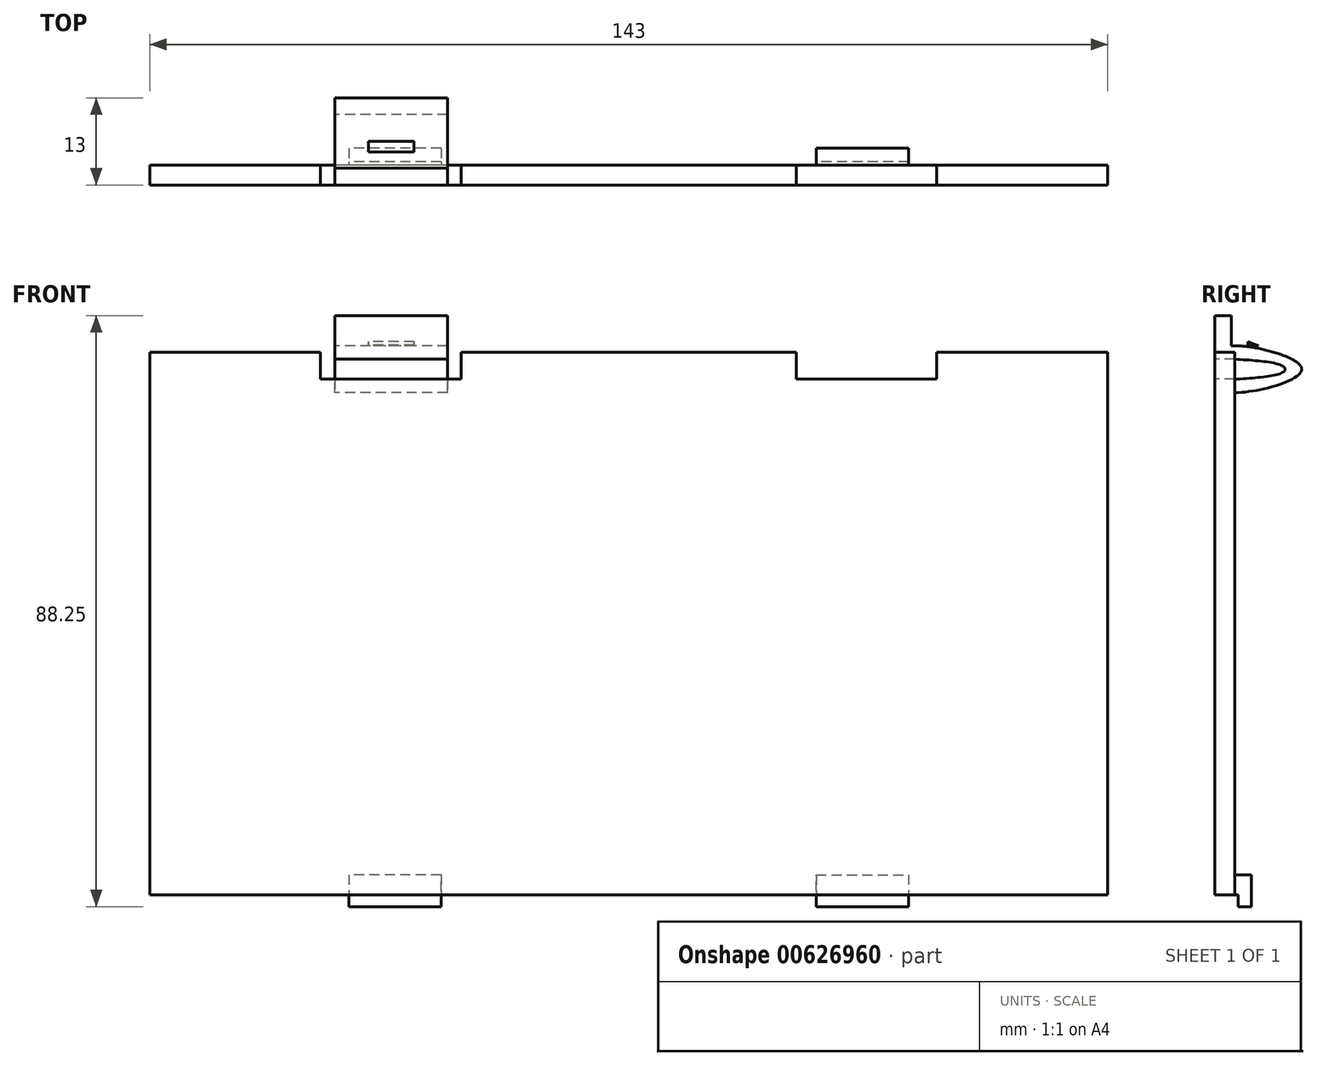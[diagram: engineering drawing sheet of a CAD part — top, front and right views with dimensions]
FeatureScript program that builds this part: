
annotation { "Feature Type Name" : "Feature", "Feature Type Description" : "" }
export const myFeature = defineFeature(function(context is Context, id is Id, definition is map)
    precondition{}
    {
        {
            var Q0;
            Q0=qCreatedBy(makeId("Front.planeOp"),FACE);
            var sketch = newSketch(context, id + "F0", { "sketchPlane" : qUnion([Q0])});
            skLineSegment(sketch, "E0.bottom", {"start": v(71.5, 40.5) * mm, "end": v(-71.5, 40.5) * mm});
            skLineSegment(sketch, "E0.top", {"start": v(71.5, -40.5) * mm, "end": v(-71.5, -40.5) * mm});
            skLineSegment(sketch, "E0.left", {"start": v(71.5, 40.5) * mm, "end": v(71.5, -40.5) * mm});
            skLineSegment(sketch, "E0.right", {"start": v(-71.5, 40.5) * mm, "end": v(-71.5, -40.5) * mm});
            skPoint(sketch, "E0.middle", {"position": v(0, 0) * mm});
            skSolve(sketch);
        }
        {
            var Q0;
            Q0=makeQuery(id+"F0.imprint","IMPRINT",FACE,{"disambiguationData":[TD([[makeQuery(id+"F0.imprint","IMPRINT",EDGE,{"derivedFrom":sQuery(id+"F0.wireOp",EDGE,"E0.bottom")}),1.0]])]});
            extrude(context, id + "F1", {"entities" : qUnion([Q0]), "depth" : 3 * mm});
        }
        {
            var Q0;
            Q0=makeQuery(id+"F1.opExtrude","CAP_FACE",FACE,{"disambiguationData":[OSD([sQuery(id+"F0.wireOp",EDGE,"E0.bottom"),sQuery(id+"F0.wireOp",EDGE,"E0.top"),sQuery(id+"F0.wireOp",EDGE,"E0.left"),sQuery(id+"F0.wireOp",EDGE,"E0.right")])],"isStart":true});
            var sketch = newSketch(context, id + "F2", { "sketchPlane" : qUnion([Q0])});
            skLineSegment(sketch, "E1", {"start": v(-28, -40.5) * mm, "end": v(-28, 40.5) * mm, "construction": true});
            skLineSegment(sketch, "E2", {"start": v(-28, 0) * mm, "end": v(0, 0) * mm, "construction": true});
            skLineSegment(sketch, "E3", {"start": v(0, 0) * mm, "end": v(28, 0) * mm, "construction": true});
            skLineSegment(sketch, "E4", {"start": v(28, 40.5) * mm, "end": v(28, -40.5) * mm, "construction": true});
            skLineSegment(sketch, "E5", {"start": v(-28, -37.5) * mm, "end": v(-41.8, -37.5) * mm});
            skLineSegment(sketch, "E6", {"start": v(-41.8, -37.5) * mm, "end": v(-41.8, -40.5) * mm});
            skLineSegment(sketch, "E7", {"start": v(-41.8, -40.5) * mm, "end": v(-28, -40.5) * mm});
            skLineSegment(sketch, "E8", {"start": v(-28, -37.5) * mm, "end": v(-28, -40.5) * mm});
            skLineSegment(sketch, "E9.MirrorCS", {"start": v(41.8, -40.5) * mm, "end": v(28, -40.5) * mm});
            skLineSegment(sketch, "E10.MirrorCS", {"start": v(41.8, -37.5) * mm, "end": v(41.8, -40.5) * mm});
            skLineSegment(sketch, "E11.MirrorCS", {"start": v(28, -37.5) * mm, "end": v(41.8, -37.5) * mm});
            skLineSegment(sketch, "E12", {"start": v(28, -37.5) * mm, "end": v(28, -40.5) * mm});
            skSolve(sketch);
        }
        {
            var Q0;
            Q0=makeQuery(id+"F2.imprint","IMPRINT",FACE,{"disambiguationData":[TD([[makeQuery(id+"F2.imprint","IMPRINT",EDGE,{"derivedFrom":sQuery(id+"F2.wireOp",EDGE,"E5")}),1.0]])]});
            var Q1;
            Q1=makeQuery(id+"F2.imprint","IMPRINT",FACE,{"disambiguationData":[TD([[makeQuery(id+"F2.imprint","IMPRINT",EDGE,{"derivedFrom":sQuery(id+"F2.wireOp",EDGE,"E9.MirrorCS")}),1.0]])]});
            extrude(context, id + "F3", {"entities" : qUnion([Q0, Q1]), "operationType" : NewBodyOperationType.ADD, "depth" : 0.5 * mm});
        }
        {
            var Q0;
            Q0=makeQuery(id+"F3.opExtrude","CAP_FACE",FACE,{"disambiguationData":[OSD([sQuery(id+"F2.wireOp",EDGE,"E5"),sQuery(id+"F2.wireOp",EDGE,"E6"),sQuery(id+"F2.wireOp",EDGE,"E7"),sQuery(id+"F2.wireOp",EDGE,"E8")])],"isStart":false});
            var sketch = newSketch(context, id + "F4", { "sketchPlane" : qUnion([Q0])});
            skLineSegment(sketch, "E13.0", {"start": v(-28, -37.5) * mm, "end": v(-41.8, -37.5) * mm});
            skLineSegment(sketch, "E14", {"start": v(-41.8, -37.5) * mm, "end": v(-41.8, -42.25) * mm});
            skLineSegment(sketch, "E15", {"start": v(-41.8, -42.25) * mm, "end": v(-28, -42.25) * mm});
            skLineSegment(sketch, "E16", {"start": v(-28, -42.25) * mm, "end": v(-28, -37.5) * mm});
            skLineSegment(sketch, "E17.MirrorCS", {"start": v(28, -42.25) * mm, "end": v(28, -37.5) * mm});
            skLineSegment(sketch, "E18.MirrorCS", {"start": v(28, -37.5) * mm, "end": v(41.8, -37.5) * mm});
            skLineSegment(sketch, "E19.MirrorCS", {"start": v(41.8, -42.25) * mm, "end": v(28, -42.25) * mm});
            skLineSegment(sketch, "E20.MirrorCS", {"start": v(41.8, -37.5) * mm, "end": v(41.8, -42.25) * mm});
            skSolve(sketch);
        }
        {
            var Q0;
            {var subQ2=sQuery(id+"F4.wireOp",EDGE,"E15");Q0=makeQuery(id+"F4.imprint","IMPRINT",FACE,{"disambiguationData":[TD([[makeQuery(id+"F4.imprint","IMPRINT",EDGE,{"derivedFrom":subQ2}),1.0]])]});}
            var Q1;
            {var subQ0=sQuery(id+"F4.wireOp",EDGE,"E13.0");Q1=makeQuery(id+"F4.imprint","IMPRINT",FACE,{"disambiguationData":[TD([[makeQuery(id+"F4.imprint","IMPRINT",EDGE,{"derivedFrom":subQ0}),1.0]])]});}
            var Q2;
            Q2=makeQuery(id+"F4.imprint","IMPRINT",FACE,{"disambiguationData":[TD([[makeQuery(id+"F4.imprint","IMPRINT",EDGE,{"derivedFrom":sQuery(id+"F4.wireOp",EDGE,"E17.MirrorCS")}),-1.0]])]});
            extrude(context, id + "F5", {"entities" : qUnion([Q0, Q1, Q2]), "operationType" : NewBodyOperationType.ADD, "depth" : 2 * mm});
        }
        {
            var Q0;
            Q0=makeQuery(id+"F1.opExtrude","CAP_FACE",FACE,{"disambiguationData":[OSD([sQuery(id+"F0.wireOp",EDGE,"E0.bottom"),sQuery(id+"F0.wireOp",EDGE,"E0.top"),sQuery(id+"F0.wireOp",EDGE,"E0.left"),sQuery(id+"F0.wireOp",EDGE,"E0.right")])],"isStart":false});
            var sketch = newSketch(context, id + "F6", { "sketchPlane" : qUnion([Q0])});
            skLineSegment(sketch, "E21", {"start": v(-25, 40.5) * mm, "end": v(-25, -40.5) * mm, "construction": true});
            skLineSegment(sketch, "E22", {"start": v(25, 40.5) * mm, "end": v(25, -40.5) * mm, "construction": true});
            skLineSegment(sketch, "E23", {"start": v(-25, 0) * mm, "end": v(0, 0) * mm, "construction": true});
            skLineSegment(sketch, "E24", {"start": v(25, 0) * mm, "end": v(0, 0) * mm, "construction": true});
            skLineSegment(sketch, "E25", {"start": v(-25, 40.5) * mm, "end": v(-25, 36.5) * mm});
            skLineSegment(sketch, "E26", {"start": v(-25, 36.5) * mm, "end": v(-46, 36.5) * mm});
            skLineSegment(sketch, "E27", {"start": v(-46, 36.5) * mm, "end": v(-46, 40.5) * mm});
            skLineSegment(sketch, "E28", {"start": v(-46, 40.5) * mm, "end": v(-25, 40.5) * mm});
            skLineSegment(sketch, "E29", {"start": v(25, 40.5) * mm, "end": v(25, 36.5) * mm});
            skLineSegment(sketch, "E30", {"start": v(25, 36.5) * mm, "end": v(46, 36.5) * mm});
            skLineSegment(sketch, "E31", {"start": v(46, 36.5) * mm, "end": v(46, 40.5) * mm});
            skLineSegment(sketch, "E32", {"start": v(46, 40.5) * mm, "end": v(25, 40.5) * mm});
            skLineSegment(sketch, "E33", {"start": v(-43.85, 36.5) * mm, "end": v(-43.85, 40.5) * mm, "construction": true});
            skLineSegment(sketch, "E34", {"start": v(-27.15, 36.5) * mm, "end": v(-27.15, 40.5) * mm, "construction": true});
            skLineSegment(sketch, "E35", {"start": v(-35.5, 40.5) * mm, "end": v(-35.5, 36.5) * mm, "construction": true});
            skLineSegment(sketch, "E36", {"start": v(-43.85, 38.5) * mm, "end": v(-35.5, 38.5) * mm, "construction": true});
            skLineSegment(sketch, "E37", {"start": v(-35.5, 38.5) * mm, "end": v(-27.15, 38.5) * mm, "construction": true});
            skSolve(sketch);
        }
        {
            var Q0;
            Q0=makeQuery(id+"F6.imprint","IMPRINT",FACE,{"disambiguationData":[TD([[makeQuery(id+"F6.imprint","IMPRINT",EDGE,{"derivedFrom":sQuery(id+"F6.wireOp",EDGE,"E25")}),-1.0]])]});
            var Q1;
            Q1=makeQuery(id+"F6.imprint","IMPRINT",FACE,{"disambiguationData":[TD([[makeQuery(id+"F6.imprint","IMPRINT",EDGE,{"derivedFrom":sQuery(id+"F6.wireOp",EDGE,"E29")}),1.0]])]});
            extrude(context, id + "F7", {"entities" : qUnion([Q0, Q1]), "operationType" : NewBodyOperationType.REMOVE, "endBound" : BoundingType.THROUGH_ALL, "oppositeDirection" : true, "depth" : 25 * mm});
        }
        {
            var Q0;
            Q0=qCreatedBy(makeId("Right.planeOp"),FACE);
            var Q1;
            Q1=sQuery(id+"F6.wireOp",VERTEX,"E33.start");
            cPlane(context, id + "F8", {"entities" : qUnion([Q0, Q1]), "cplaneType" : CPlaneType.PLANE_POINT, "offset" : 25 * mm, "width" : 150 * mm, "height" : 150 * mm});
        }
        {
            var Q0;
            Q0=qCreatedBy(id+"F8.planeOp",FACE);
            var sketch = newSketch(context, id + "F9", { "sketchPlane" : qUnion([Q0])});
            skPoint(sketch, "E38.0", {"position": v(-3, 36.5) * mm});
            skLineSegment(sketch, "E39", {"start": v(-3, 36.5) * mm, "end": v(0, 36.5) * mm});
            skLineSegment(sketch, "E40", {"start": v(0, 36.5) * mm, "end": v(0, 34.5) * mm});
            skLineSegment(sketch, "E41", {"start": v(0, 34.5) * mm, "end": v(10, 34.5) * mm, "construction": true});
            skLineSegment(sketch, "E42", {"start": v(10, 34.5) * mm, "end": v(10, 41.5) * mm, "construction": true});
            skLineSegment(sketch, "E43", {"start": v(10, 41.5) * mm, "end": v(0, 41.5) * mm, "construction": true});
            skLineSegment(sketch, "E44", {"start": v(0, 34.5) * mm, "end": v(0, 41.5) * mm, "construction": true});
            skLineSegment(sketch, "E45", {"start": v(10, 38) * mm, "end": v(0, 38) * mm, "construction": true});
            skLineSegment(sketch, "E46", {"start": v(7.5, 41.5) * mm, "end": v(7.5, 34.5) * mm, "construction": true});
            skFitSpline(sketch, "E47", {"points": [v(0, 34.5) * mm, v(10, 38) * mm], "startDerivative": vector(10.93, 0) * mm, "endDerivative": vector(0, 4.98) * mm});
            skFitSpline(sketch, "E48", {"points": [v(0, 36.5) * mm, v(7.5, 38) * mm], "startDerivative": vector(9.31, 0.6) * mm, "endDerivative": vector(0, 3.2) * mm});
            skFitSpline(sketch, "E49.MirrorCS", {"points": [v(0, 39.5) * mm, v(7.5, 38) * mm], "startDerivative": vector(9.31, -0.6) * mm, "endDerivative": vector(0, -3.2) * mm});
            skFitSpline(sketch, "E50.MirrorCS", {"points": [v(0, 41.5) * mm, v(10, 38) * mm], "startDerivative": vector(10.93, 0) * mm, "endDerivative": vector(0, -4.98) * mm});
            skLineSegment(sketch, "E51", {"start": v(0, 39.5) * mm, "end": v(0, 41.5) * mm});
            skLineSegment(sketch, "E52", {"start": v(0, 39.5) * mm, "end": v(-3, 39.5) * mm});
            skLineSegment(sketch, "E53", {"start": v(-3, 39.5) * mm, "end": v(-3, 46) * mm});
            skLineSegment(sketch, "E54", {"start": v(-3, 46) * mm, "end": v(-0.5, 46) * mm});
            skLineSegment(sketch, "E55", {"start": v(-0.5, 46) * mm, "end": v(-0.5, 41.5) * mm});
            skLineSegment(sketch, "E56", {"start": v(-0.5, 41.5) * mm, "end": v(0, 41.5) * mm});
            skLineSegment(sketch, "E57", {"start": v(7.32, 40.03) * mm, "end": v(1.94, 42.13) * mm});
            skLineSegment(sketch, "E58", {"start": v(1.94, 42.13) * mm, "end": v(1.94, 41.36) * mm});
            skSolve(sketch);
        }
        {
            var Q0;
            Q0=makeQuery(id+"F9.imprint","IMPRINT",FACE,{"disambiguationData":[TD([[makeQuery(id+"F9.imprint","IMPRINT",EDGE,{"derivedFrom":sQuery(id+"F9.wireOp",EDGE,"E40")}),1.0]])]});
            var Q1;
            Q1=makeQuery(id+"F9.imprint","IMPRINT",FACE,{"disambiguationData":[TD([[makeQuery(id+"F9.imprint","IMPRINT",EDGE,{"derivedFrom":sQuery(id+"F9.wireOp",EDGE,"E51")}),1.0]])]});
            extrude(context, id + "F10", {"entities" : qUnion([Q0, Q1]), "operationType" : NewBodyOperationType.ADD, "depth" : 16.8 * mm});
        }
        {
            var Q0;
            Q0=makeQuery(id+"F10.opExtrude","SWEPT_FACE",FACE,{"disambiguationData":[OSD([sQuery(id+"F9.wireOp",EDGE,"E56")])]});
            var sketch = newSketch(context, id + "F11", { "sketchPlane" : qUnion([Q0])});
            skLineSegment(sketch, "E59", {"start": v(-38.85, 0) * mm, "end": v(-38.85, 7.32) * mm, "construction": true});
            skLineSegment(sketch, "E60", {"start": v(-35.45, 0) * mm, "end": v(-35.45, 7.32) * mm, "construction": true});
            skLineSegment(sketch, "E61", {"start": v(-32.05, 0) * mm, "end": v(-32.05, 7.32) * mm, "construction": true});
            skLineSegment(sketch, "E62", {"start": v(-38.85, 7.32) * mm, "end": v(-35.45, 7.32) * mm});
            skLineSegment(sketch, "E63", {"start": v(-35.45, 7.32) * mm, "end": v(-32.05, 7.32) * mm});
            skPoint(sketch, "E64.0", {"position": v(-43.85, 7.32) * mm});
            skSolve(sketch);
        }
        {
            var Q0;
            Q0=makeQuery(id+"F9.imprint","IMPRINT",FACE,{"disambiguationData":[TD([[makeQuery(id+"F9.imprint","IMPRINT",EDGE,{"derivedFrom":sQuery(id+"F9.wireOp",EDGE,"E51")}),1.0]])]});
            var Q1;
            Q1=sQuery(id+"F11.wireOp",VERTEX,"E59.end");
            cPlane(context, id + "F12", {"entities" : qUnion([Q0, Q1]), "cplaneType" : CPlaneType.PLANE_POINT, "offset" : 25 * mm, "width" : 150 * mm, "height" : 150 * mm});
        }
        {
            var Q0;
            Q0=qCreatedBy(id+"F12.planeOp",FACE);
            var sketch = newSketch(context, id + "F13", { "sketchPlane" : qUnion([Q0])});
            skFitSpline(sketch, "E65.0", {"points": [v(0, 41.5) * mm, v(3.64, 41.5) * mm, v(10, 39.66) * mm, v(10, 38) * mm]});
            skLineSegment(sketch, "E65.1", {"start": v(7.32, 40.03) * mm, "end": v(1.94, 42.13) * mm});
            skLineSegment(sketch, "E65.2", {"start": v(1.94, 42.13) * mm, "end": v(1.94, 41.36) * mm});
            skPoint(sketch, "E66.orphan", {"position": v(10, 38) * mm});
            skPoint(sketch, "E67.orphan", {"position": v(0, 41.5) * mm});
            skSolve(sketch);
        }
        {
            var Q0;
            Q0=makeQuery(id+"F13.imprint","IMPRINT",FACE,{"disambiguationData":[TD([[makeQuery(id+"F13.imprint","IMPRINT",EDGE,{"derivedFrom":sQuery(id+"F13.wireOp",EDGE,"E65.0")}),1.0]])]});
            extrude(context, id + "F14", {"entities" : qUnion([Q0]), "operationType" : NewBodyOperationType.ADD, "depth" : 6.8 * mm});
        }
    });
